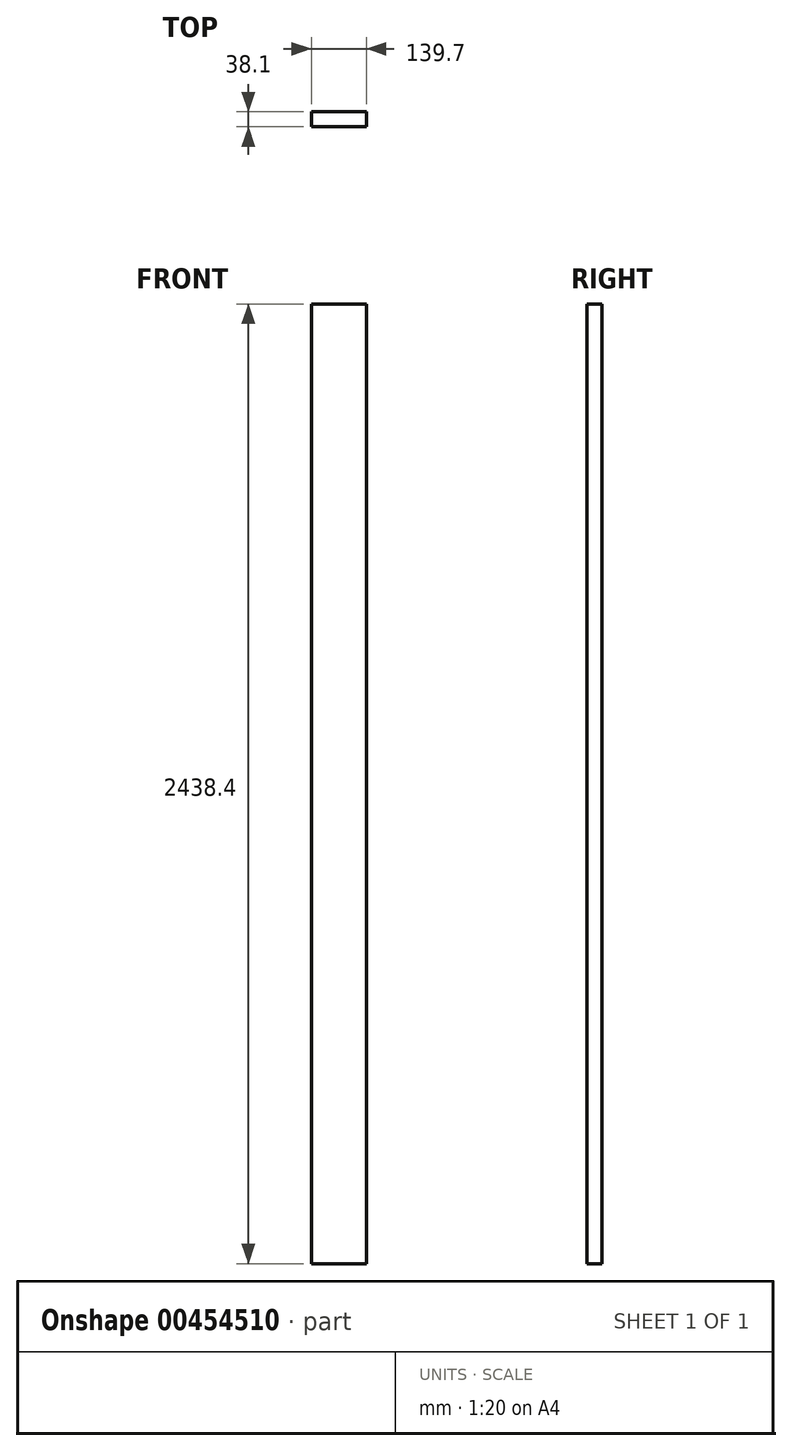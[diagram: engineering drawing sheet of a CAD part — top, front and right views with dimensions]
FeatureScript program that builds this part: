
annotation { "Feature Type Name" : "Feature", "Feature Type Description" : "" }
export const myFeature = defineFeature(function(context is Context, id is Id, definition is map)
    precondition{}
    {
        {
            var Q0;
            Q0=qCreatedBy(makeId("Top.planeOp"),FACE);
            var sketch = newSketch(context, id + "F0", { "sketchPlane" : qUnion([Q0])});
            skLineSegment(sketch, "E0.bottom", {"start": v(0, 0) * mm, "end": v(139.7, 0) * mm});
            skLineSegment(sketch, "E0.top", {"start": v(0, 38.1) * mm, "end": v(139.7, 38.1) * mm});
            skLineSegment(sketch, "E0.left", {"start": v(0, 0) * mm, "end": v(0, 38.1) * mm});
            skLineSegment(sketch, "E0.right", {"start": v(139.7, 0) * mm, "end": v(139.7, 38.1) * mm});
            skSolve(sketch);
        }
        {
            var Q0;
            Q0=qSketchRegion(id+"F0",true);
            extrude(context, id + "F1", {"entities" : qUnion([Q0]), "depth" : 2438.4 * mm});
        }
    });
